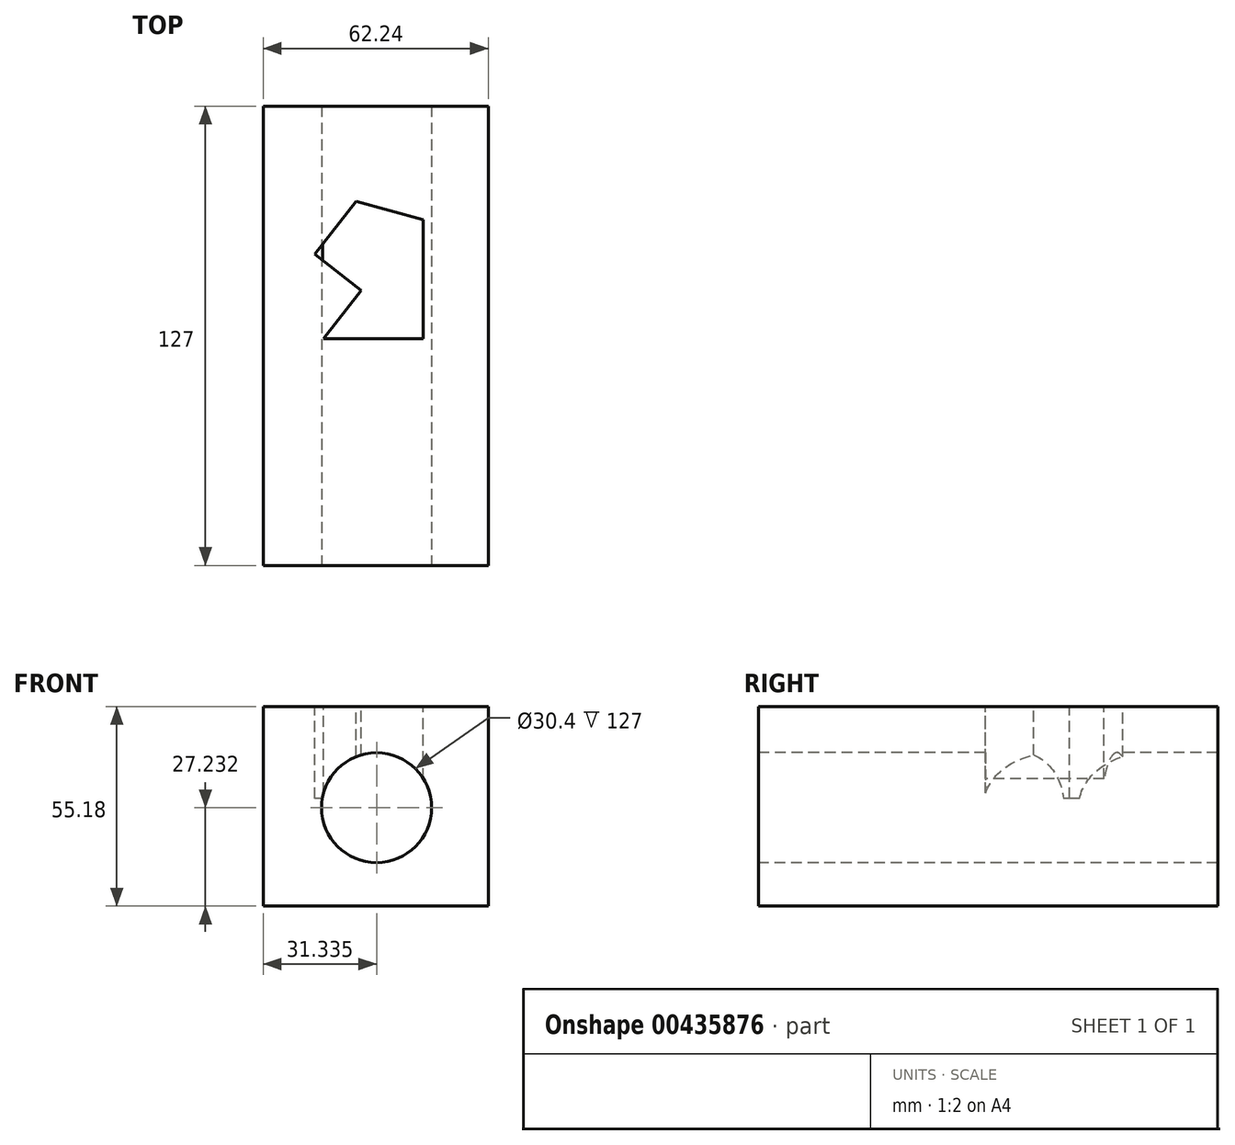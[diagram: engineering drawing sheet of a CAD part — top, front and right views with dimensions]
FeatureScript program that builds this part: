
annotation { "Feature Type Name" : "Feature", "Feature Type Description" : "" }
export const myFeature = defineFeature(function(context is Context, id is Id, definition is map)
    precondition{}
    {
        {
            var Q0;
            Q0=qCreatedBy(makeId("Front.planeOp"),FACE);
            var sketch = newSketch(context, id + "F0", { "sketchPlane" : qUnion([Q0])});
            skLineSegment(sketch, "E0.bottom", {"start": v(0, 0) * mm, "end": v(62.24, 0) * mm});
            skLineSegment(sketch, "E0.top", {"start": v(0, 55.18) * mm, "end": v(62.24, 55.18) * mm});
            skLineSegment(sketch, "E0.left", {"start": v(0, 0) * mm, "end": v(0, 55.18) * mm});
            skLineSegment(sketch, "E0.right", {"start": v(62.24, 0) * mm, "end": v(62.24, 55.18) * mm});
            skSolve(sketch);
        }
        {
            var Q0;
            Q0 = qSketchRegion(id + "F0", true);
            extrude(context, id + "F1", {"entities" : qUnion([Q0]), "depth" : 127 * mm});
        }
        {
            var Q0;
            Q0=makeQuery(id+"F1.opExtrude","CAP_FACE",FACE,{"disambiguationData":[OSD([sQuery(id+"F0.wireOp",EDGE,"E0.bottom"),sQuery(id+"F0.wireOp",EDGE,"E0.top"),sQuery(id+"F0.wireOp",EDGE,"E0.left"),sQuery(id+"F0.wireOp",EDGE,"E0.right")])],"isStart":false});
            var sketch = newSketch(context, id + "F2", { "sketchPlane" : qUnion([Q0])});
            skCircle(sketch, "E1", {"center": v(31.33, 27.23) * mm, "radius": 15.2 * mm});
            skSolve(sketch);
        }
        {
            var Q0;
            Q0 = qSketchRegion(id + "F2", true);
            extrude(context, id + "F3", {"entities" : qUnion([Q0]), "operationType" : NewBodyOperationType.REMOVE, "oppositeDirection" : true, "depth" : 127 * mm});
        }
        {
            var Q0;
            Q0=makeQuery(id+"F1.opExtrude","SWEPT_FACE",FACE,{"disambiguationData":[OSD([sQuery(id+"F0.wireOp",EDGE,"E0.top")])]});
            var sketch = newSketch(context, id + "F4", { "sketchPlane" : qUnion([Q0])});
            skLineSegment(sketch, "E2", {"start": v(25.64, -26.33) * mm, "end": v(14.24, -40.97) * mm});
            skLineSegment(sketch, "E3", {"start": v(14.24, -40.97) * mm, "end": v(27.03, -50.94) * mm});
            skLineSegment(sketch, "E4", {"start": v(27.03, -50.94) * mm, "end": v(16.67, -64.24) * mm});
            skLineSegment(sketch, "E5", {"start": v(16.67, -64.24) * mm, "end": v(44.28, -64.24) * mm});
            skLineSegment(sketch, "E6", {"start": v(44.28, -64.24) * mm, "end": v(44.28, -31.43) * mm});
            skLineSegment(sketch, "E7", {"start": v(44.28, -31.43) * mm, "end": v(25.64, -26.33) * mm});
            skSolve(sketch);
        }
        {
            var Q0;
            Q0 = qSketchRegion(id + "F4", true);
            extrude(context, id + "F5", {"entities" : qUnion([Q0]), "operationType" : NewBodyOperationType.REMOVE, "oppositeDirection" : true, "depth" : 25.4 * mm});
        }
    });
